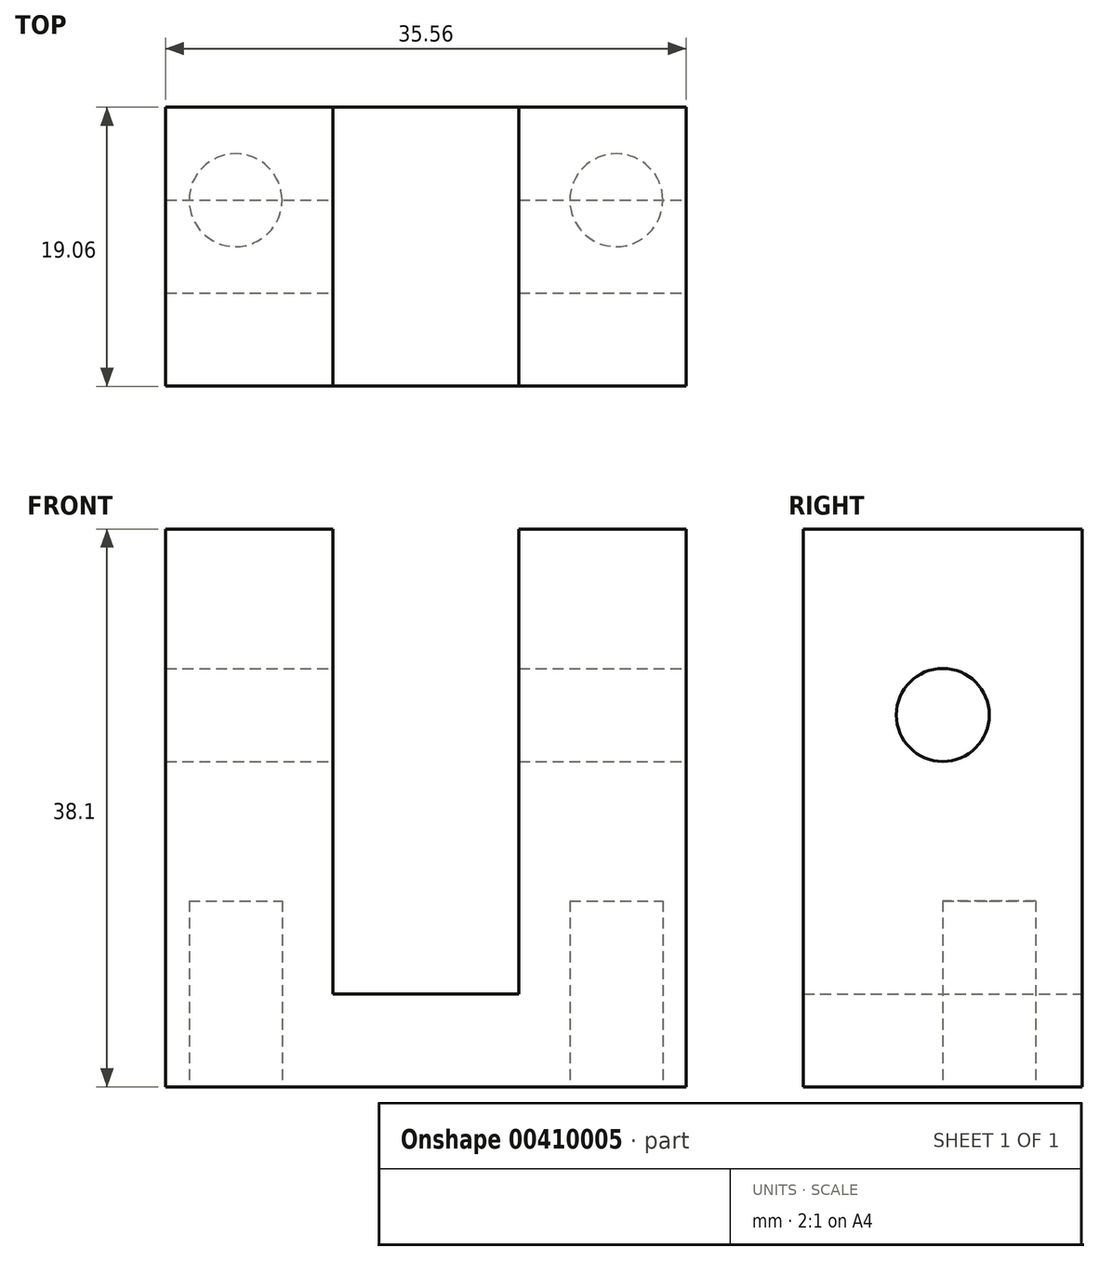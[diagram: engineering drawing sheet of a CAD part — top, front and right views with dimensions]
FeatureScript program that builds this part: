
annotation { "Feature Type Name" : "Feature", "Feature Type Description" : "" }
export const myFeature = defineFeature(function(context is Context, id is Id, definition is map)
    precondition{}
    {
        {
            var Q0;
            Q0=qCreatedBy(makeId("Front.planeOp"),FACE);
            var sketch = newSketch(context, id + "F0", { "sketchPlane" : qUnion([Q0])});
            skLineSegment(sketch, "E0", {"start": v(0, 28.33) * mm, "end": v(0, -29.63) * mm, "construction": true});
            skLineSegment(sketch, "E1", {"start": v(0, -19.05) * mm, "end": v(-6.35, -19.05) * mm});
            skLineSegment(sketch, "E2", {"start": v(-6.35, -19.05) * mm, "end": v(-6.35, 12.7) * mm});
            skLineSegment(sketch, "E3", {"start": v(-6.35, 12.7) * mm, "end": v(-17.78, 12.7) * mm});
            skLineSegment(sketch, "E4", {"start": v(-17.78, 12.7) * mm, "end": v(-17.78, -25.4) * mm});
            skLineSegment(sketch, "E5", {"start": v(-17.78, -25.4) * mm, "end": v(0, -25.4) * mm});
            skLineSegment(sketch, "E6.MirrorCS", {"start": v(6.35, -19.05) * mm, "end": v(6.35, 12.7) * mm});
            skLineSegment(sketch, "E7.MirrorCS", {"start": v(6.35, 12.7) * mm, "end": v(17.78, 12.7) * mm});
            skLineSegment(sketch, "E8.MirrorCS", {"start": v(17.78, 12.7) * mm, "end": v(17.78, -25.4) * mm});
            skLineSegment(sketch, "E9.MirrorCS", {"start": v(17.78, -25.4) * mm, "end": v(0, -25.4) * mm});
            skLineSegment(sketch, "E10.MirrorCS", {"start": v(0, -19.05) * mm, "end": v(6.35, -19.05) * mm});
            skSolve(sketch);
        }
        {
            var Q0;
            Q0=makeQuery(id+"F0.imprint","IMPRINT",FACE,{"disambiguationData":[TD([[makeQuery(id+"F0.imprint","IMPRINT",EDGE,{"derivedFrom":sQuery(id+"F0.wireOp",EDGE,"E1")}),1.0]])]});
            extrude(context, id + "F1", {"entities" : qUnion([Q0]), "endBound" : BoundingType.SYMMETRIC, "depth" : 19.05 * mm});
        }
        {
            var Q0;
            Q0=qCreatedBy(makeId("Right.planeOp"),FACE);
            var sketch = newSketch(context, id + "F2", { "sketchPlane" : qUnion([Q0])});
            skCircle(sketch, "E11", {"center": v(0, 0) * mm, "radius": 3.18 * mm});
            skSolve(sketch);
        }
        {
            var Q0;
            Q0 = qSketchRegion(id + "F2", true);
            extrude(context, id + "F3", {"entities" : qUnion([Q0]), "operationType" : NewBodyOperationType.REMOVE, "endBound" : BoundingType.SYMMETRIC, "oppositeDirection" : true, "depth" : 2540 * mm});
        }
        {
            var Q0;
            Q0=makeQuery(id+"F1.opExtrude","SWEPT_FACE",FACE,{"disambiguationData":[OSD([sQuery(id+"F0.wireOp",EDGE,"E5"),sQuery(id+"F0.wireOp",EDGE,"E9.MirrorCS")])]});
            var sketch = newSketch(context, id + "F4", { "sketchPlane" : qUnion([Q0])});
            skLineSegment(sketch, "E12", {"start": v(0, -21.72) * mm, "end": v(0, 22.8) * mm, "construction": true});
            skLineSegment(sketch, "E13", {"start": v(28.67, -3.17) * mm, "end": v(-33.23, -3.18) * mm, "construction": true});
            skCircle(sketch, "E14", {"center": v(13, -3.17) * mm, "radius": 3.18 * mm});
            skCircle(sketch, "E15.MirrorC", {"center": v(-13, -3.17) * mm, "radius": 3.18 * mm});
            skSolve(sketch);
        }
        {
            var Q0;
            Q0 = qSketchRegion(id + "F4", true);
            extrude(context, id + "F5", {"entities" : qUnion([Q0]), "operationType" : NewBodyOperationType.REMOVE, "oppositeDirection" : true, "depth" : 12.7 * mm});
        }
    });
